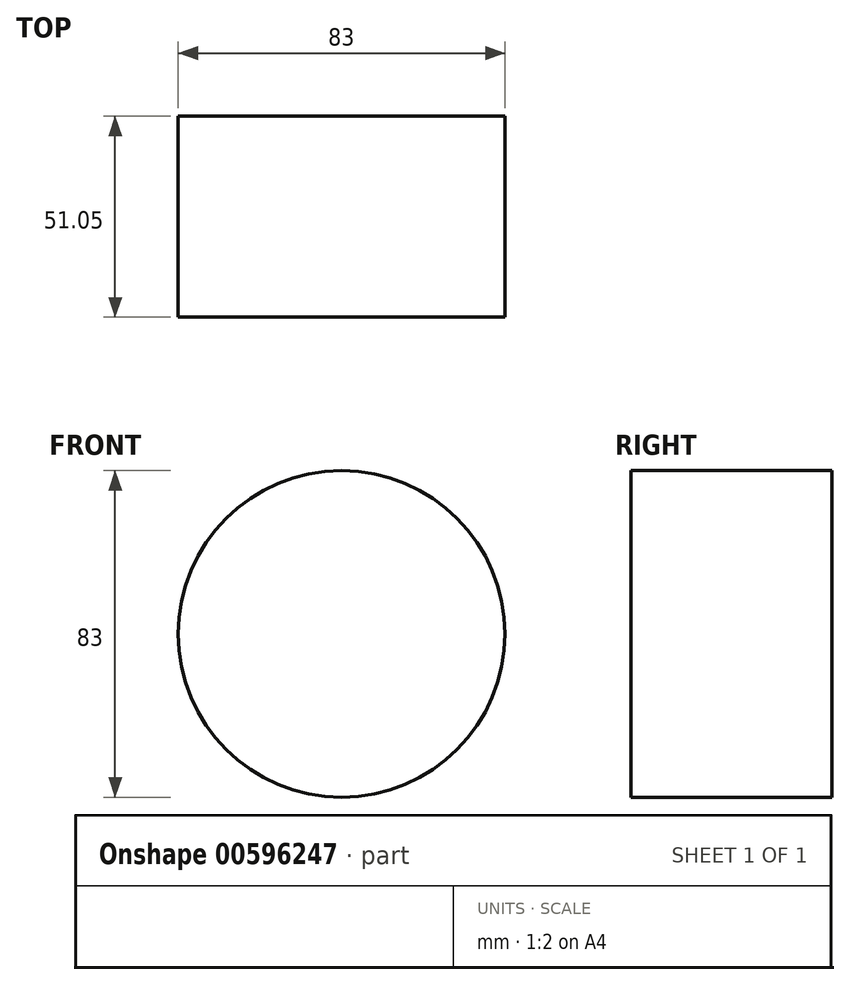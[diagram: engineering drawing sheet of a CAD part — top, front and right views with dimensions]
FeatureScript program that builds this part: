
annotation { "Feature Type Name" : "Feature", "Feature Type Description" : "" }
export const myFeature = defineFeature(function(context is Context, id is Id, definition is map)
    precondition{}
    {
        {
            var Q0;
            Q0=qCreatedBy(makeId("Front.planeOp"),FACE);
            var sketch = newSketch(context, id + "F0", { "sketchPlane" : qUnion([Q0])});
            skCircle(sketch, "E0", {"center": v(-21.15, 14.03) * mm, "radius": 41.5 * mm});
            skSolve(sketch);
        }
        {
            var Q0;
            Q0=sQuery(id+"F0.wireOp",EDGE,"E0");
            extrude(context, id + "F1", {"bodyType" : ToolBodyType.SURFACE, "surfaceEntities" : qUnion([Q0]), "depth" : 51.05 * mm, "offsetDistance" : 25.4 * mm});
        }
    });
